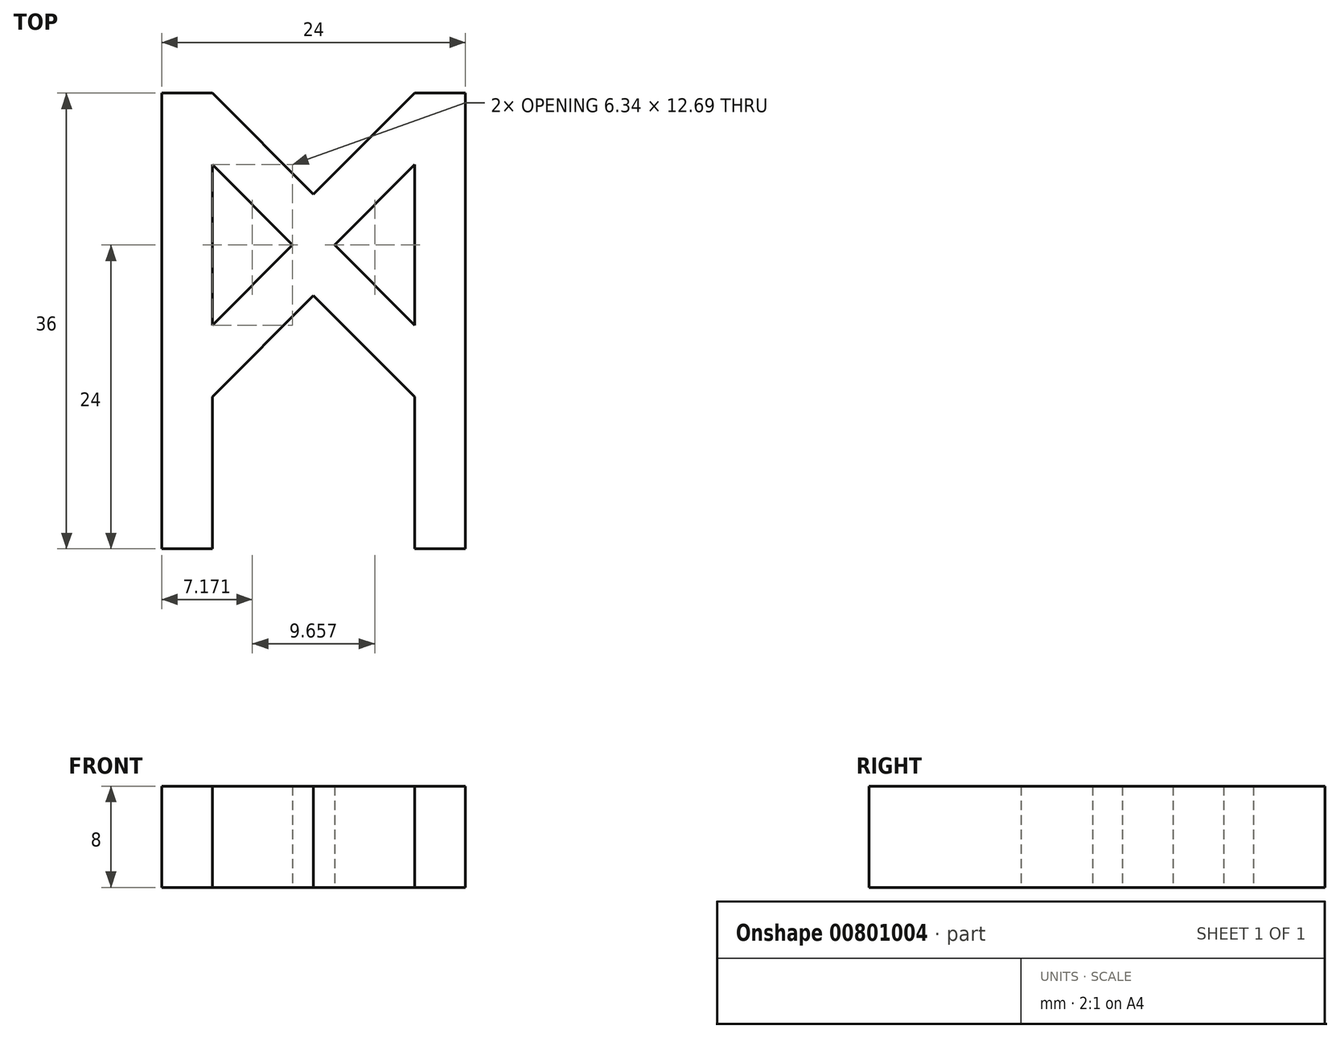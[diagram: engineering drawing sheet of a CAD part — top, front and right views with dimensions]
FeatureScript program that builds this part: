
annotation { "Feature Type Name" : "Feature", "Feature Type Description" : "" }
export const myFeature = defineFeature(function(context is Context, id is Id, definition is map)
    precondition{}
    {
        {
            var Q0;
            Q0=qCreatedBy(makeId("Top.planeOp"),FACE);
            var sketch = newSketch(context, id + "F0", { "sketchPlane" : qUnion([Q0])});
            skLineSegment(sketch, "E0", {"start": v(4, -24) * mm, "end": v(12, -16) * mm});
            skLineSegment(sketch, "E1", {"start": v(12, -16) * mm, "end": v(20, -24) * mm});
            skLineSegment(sketch, "E2", {"start": v(24, 0) * mm, "end": v(20, 0) * mm});
            skLineSegment(sketch, "E3", {"start": v(20, 0) * mm, "end": v(12, -8) * mm});
            skLineSegment(sketch, "E4", {"start": v(12, -8) * mm, "end": v(4, 0) * mm});
            skLineSegment(sketch, "E5", {"start": v(4, 0) * mm, "end": v(0, 0) * mm});
            skLineSegment(sketch, "E6", {"start": v(4, -18.34) * mm, "end": v(10.34, -12) * mm});
            skLineSegment(sketch, "E7", {"start": v(10.34, -12) * mm, "end": v(4, -5.66) * mm});
            skLineSegment(sketch, "E8", {"start": v(4, -5.66) * mm, "end": v(4, -18.34) * mm});
            skLineSegment(sketch, "E9", {"start": v(12, -8) * mm, "end": v(12, -16) * mm, "construction": true});
            skLineSegment(sketch, "E10.MirrorCS", {"start": v(13.66, -12) * mm, "end": v(20, -5.66) * mm});
            skLineSegment(sketch, "E11.MirrorCS", {"start": v(20, -5.66) * mm, "end": v(20, -18.34) * mm});
            skLineSegment(sketch, "E12.MirrorCS", {"start": v(20, -18.34) * mm, "end": v(13.66, -12) * mm});
            skLineSegment(sketch, "E13", {"start": v(0, -36) * mm, "end": v(4, -36) * mm});
            skLineSegment(sketch, "E14", {"start": v(4, -36) * mm, "end": v(4, -24) * mm});
            skLineSegment(sketch, "E15", {"start": v(20, -24) * mm, "end": v(20, -36) * mm});
            skLineSegment(sketch, "E16", {"start": v(20, -36) * mm, "end": v(24, -36) * mm});
            skLineSegment(sketch, "E17", {"start": v(24, -36) * mm, "end": v(24, 0) * mm});
            skLineSegment(sketch, "E18", {"start": v(0, -36) * mm, "end": v(0, 0) * mm});
            skSolve(sketch);
        }
        {
            var Q0;
            Q0=makeQuery(id+"F0.imprint","IMPRINT",FACE,{"disambiguationData":[TD([[makeQuery(id+"F0.imprint","IMPRINT",EDGE,{"derivedFrom":sQuery(id+"F0.wireOp",EDGE,"E0")}),1.0]])]});
            extrude(context, id + "F1", {"entities" : qUnion([Q0]), "depth" : 8 * mm, "offsetDistance" : 25 * mm});
        }
    });
